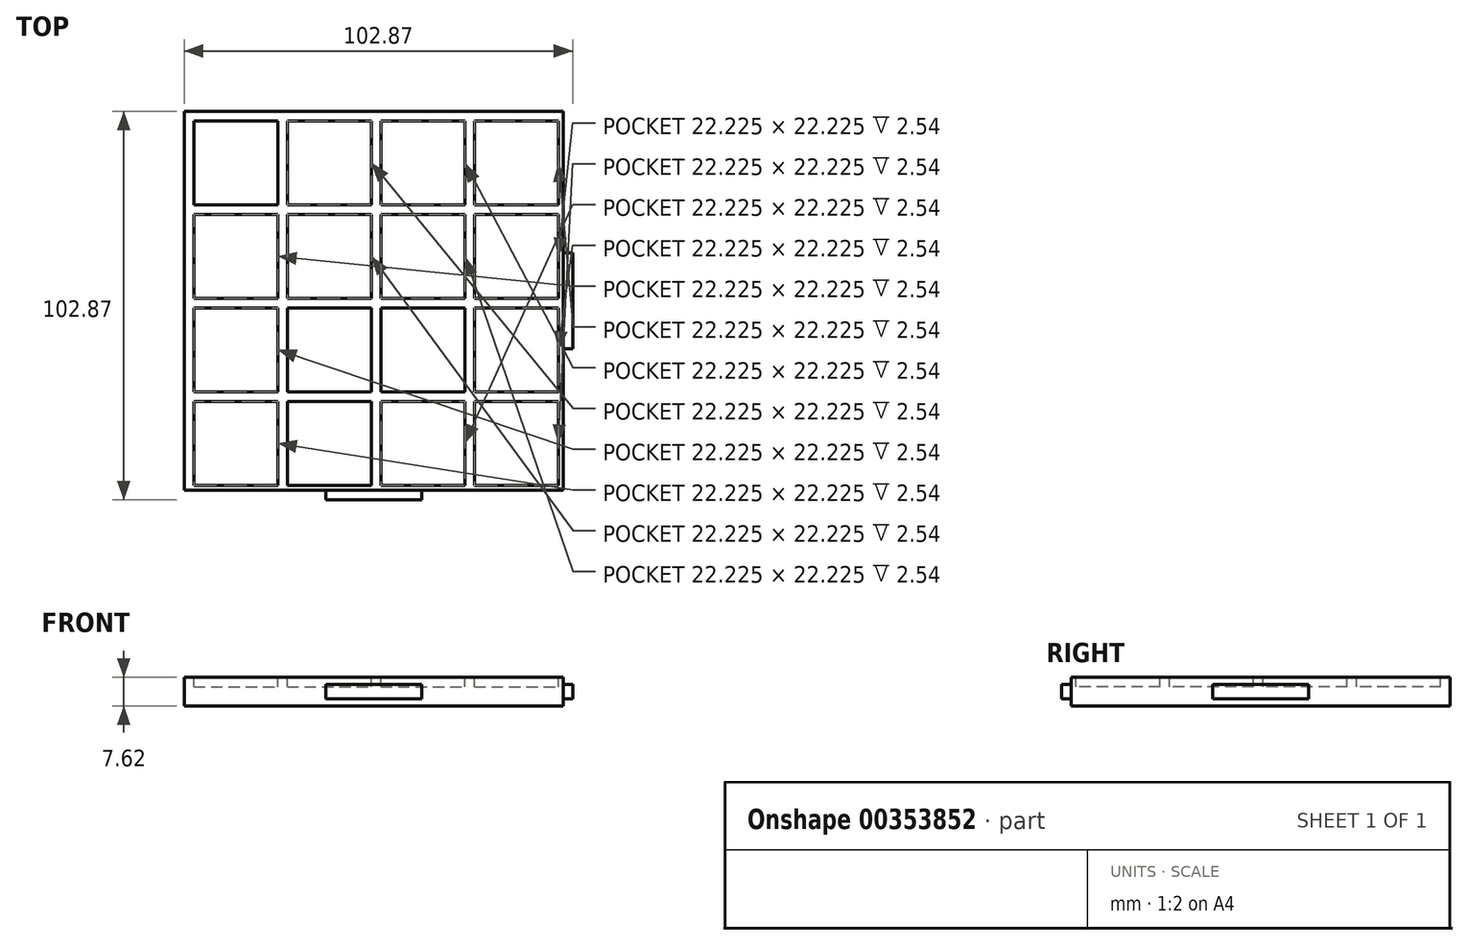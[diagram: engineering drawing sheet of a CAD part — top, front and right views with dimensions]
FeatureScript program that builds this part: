
annotation { "Feature Type Name" : "Feature", "Feature Type Description" : "" }
export const myFeature = defineFeature(function(context is Context, id is Id, definition is map)
    precondition{}
    {
        {
            var Q0;
            Q0=qCreatedBy(makeId("Top.planeOp"),FACE);
            var sketch = newSketch(context, id + "F0", { "sketchPlane" : qUnion([Q0])});
            skLineSegment(sketch, "E0.bottom", {"start": v(0, 0) * mm, "end": v(100.33, 0) * mm});
            skLineSegment(sketch, "E0.top", {"start": v(0, 100.33) * mm, "end": v(100.33, 100.33) * mm});
            skLineSegment(sketch, "E0.left", {"start": v(0, 0) * mm, "end": v(0, 100.33) * mm});
            skLineSegment(sketch, "E0.right", {"start": v(100.33, 0) * mm, "end": v(100.33, 100.33) * mm});
            skSolve(sketch);
        }
        {
            var Q0;
            Q0 = qSketchRegion(id + "F0", true);
            extrude(context, id + "F1", {"entities" : qUnion([Q0]), "oppositeDirection" : true, "depth" : 7.62 * mm});
        }
        {
            var Q0;
            Q0=qCreatedBy(makeId("Top.planeOp"),FACE);
            var sketch = newSketch(context, id + "F2", { "sketchPlane" : qUnion([Q0])});
            skLineSegment(sketch, "E1.bottom", {"start": v(2.54, 97.8) * mm, "end": v(24.77, 97.8) * mm});
            skLineSegment(sketch, "E1.top", {"start": v(2.54, 75.57) * mm, "end": v(24.77, 75.57) * mm});
            skLineSegment(sketch, "E1.left", {"start": v(2.54, 97.8) * mm, "end": v(2.54, 75.57) * mm});
            skLineSegment(sketch, "E1.right", {"start": v(24.77, 97.8) * mm, "end": v(24.77, 75.56) * mm});
            skLineSegment(sketch, "E2.bottom", {"start": v(27.3, 97.8) * mm, "end": v(49.53, 97.8) * mm});
            skLineSegment(sketch, "E2.top", {"start": v(27.3, 75.56) * mm, "end": v(49.53, 75.57) * mm});
            skLineSegment(sketch, "E2.left", {"start": v(27.3, 97.8) * mm, "end": v(27.3, 75.56) * mm});
            skLineSegment(sketch, "E2.right", {"start": v(49.53, 97.8) * mm, "end": v(49.53, 75.56) * mm});
            skLineSegment(sketch, "E3.bottom", {"start": v(52.07, 97.8) * mm, "end": v(74.3, 97.8) * mm});
            skLineSegment(sketch, "E3.top", {"start": v(52.07, 75.57) * mm, "end": v(74.3, 75.57) * mm});
            skLineSegment(sketch, "E3.left", {"start": v(52.07, 97.8) * mm, "end": v(52.07, 75.57) * mm});
            skLineSegment(sketch, "E3.right", {"start": v(74.3, 97.8) * mm, "end": v(74.3, 75.57) * mm});
            skLineSegment(sketch, "E4.bottom", {"start": v(76.84, 97.8) * mm, "end": v(99.06, 97.8) * mm});
            skLineSegment(sketch, "E4.top", {"start": v(76.84, 75.57) * mm, "end": v(99.06, 75.56) * mm});
            skLineSegment(sketch, "E4.left", {"start": v(76.84, 97.8) * mm, "end": v(76.84, 75.57) * mm});
            skLineSegment(sketch, "E4.right", {"start": v(99.06, 97.8) * mm, "end": v(99.06, 75.57) * mm});
            skLineSegment(sketch, "E5.bottom", {"start": v(2.54, 73.03) * mm, "end": v(24.77, 73.03) * mm});
            skLineSegment(sketch, "E5.top", {"start": v(2.54, 50.8) * mm, "end": v(24.76, 50.8) * mm});
            skLineSegment(sketch, "E5.left", {"start": v(2.54, 73.03) * mm, "end": v(2.54, 50.8) * mm});
            skLineSegment(sketch, "E5.right", {"start": v(24.76, 73.03) * mm, "end": v(24.76, 50.8) * mm});
            skLineSegment(sketch, "E6.bottom", {"start": v(2.54, 48.26) * mm, "end": v(24.77, 48.26) * mm});
            skLineSegment(sketch, "E6.top", {"start": v(2.54, 26.04) * mm, "end": v(24.77, 26.04) * mm});
            skLineSegment(sketch, "E6.left", {"start": v(2.54, 48.26) * mm, "end": v(2.54, 26.04) * mm});
            skLineSegment(sketch, "E6.right", {"start": v(24.77, 48.26) * mm, "end": v(24.77, 26.04) * mm});
            skLineSegment(sketch, "E7.bottom", {"start": v(2.54, 23.5) * mm, "end": v(24.77, 23.5) * mm});
            skLineSegment(sketch, "E7.top", {"start": v(2.54, 1.27) * mm, "end": v(24.76, 1.27) * mm});
            skLineSegment(sketch, "E7.left", {"start": v(2.54, 23.5) * mm, "end": v(2.54, 1.27) * mm});
            skLineSegment(sketch, "E7.right", {"start": v(24.77, 23.5) * mm, "end": v(24.77, 1.27) * mm});
            skLineSegment(sketch, "E8.bottom", {"start": v(27.3, 73.02) * mm, "end": v(49.53, 73.02) * mm});
            skLineSegment(sketch, "E8.top", {"start": v(27.3, 50.8) * mm, "end": v(49.53, 50.8) * mm});
            skLineSegment(sketch, "E8.left", {"start": v(27.3, 73.02) * mm, "end": v(27.3, 50.8) * mm});
            skLineSegment(sketch, "E8.right", {"start": v(49.53, 73.02) * mm, "end": v(49.53, 50.8) * mm});
            skLineSegment(sketch, "E9.bottom", {"start": v(52.07, 73.03) * mm, "end": v(74.3, 73.03) * mm});
            skLineSegment(sketch, "E9.top", {"start": v(52.07, 50.8) * mm, "end": v(74.3, 50.8) * mm});
            skLineSegment(sketch, "E9.left", {"start": v(52.07, 73.03) * mm, "end": v(52.07, 50.8) * mm});
            skLineSegment(sketch, "E9.right", {"start": v(74.3, 73.03) * mm, "end": v(74.3, 50.8) * mm});
            skLineSegment(sketch, "E10.bottom", {"start": v(76.83, 73.03) * mm, "end": v(99.06, 73.03) * mm});
            skLineSegment(sketch, "E10.top", {"start": v(76.83, 50.8) * mm, "end": v(99.06, 50.8) * mm});
            skLineSegment(sketch, "E10.left", {"start": v(76.83, 73.03) * mm, "end": v(76.83, 50.8) * mm});
            skLineSegment(sketch, "E10.right", {"start": v(99.06, 73.03) * mm, "end": v(99.06, 50.8) * mm});
            skLineSegment(sketch, "E11.bottom", {"start": v(27.3, 48.26) * mm, "end": v(49.53, 48.26) * mm});
            skLineSegment(sketch, "E11.top", {"start": v(27.3, 26.03) * mm, "end": v(49.53, 26.03) * mm});
            skLineSegment(sketch, "E11.left", {"start": v(27.3, 48.26) * mm, "end": v(27.3, 26.03) * mm});
            skLineSegment(sketch, "E11.right", {"start": v(49.53, 48.26) * mm, "end": v(49.53, 26.03) * mm});
            skLineSegment(sketch, "E12.bottom", {"start": v(27.3, 23.5) * mm, "end": v(49.53, 23.5) * mm});
            skLineSegment(sketch, "E12.top", {"start": v(27.3, 1.27) * mm, "end": v(49.53, 1.27) * mm});
            skLineSegment(sketch, "E12.left", {"start": v(27.3, 23.5) * mm, "end": v(27.3, 1.27) * mm});
            skLineSegment(sketch, "E12.right", {"start": v(49.53, 23.5) * mm, "end": v(49.53, 1.27) * mm});
            skLineSegment(sketch, "E13.bottom", {"start": v(52.07, 48.26) * mm, "end": v(74.3, 48.26) * mm});
            skLineSegment(sketch, "E13.top", {"start": v(52.07, 26.03) * mm, "end": v(74.3, 26.03) * mm});
            skLineSegment(sketch, "E13.left", {"start": v(52.07, 48.26) * mm, "end": v(52.07, 26.03) * mm});
            skLineSegment(sketch, "E13.right", {"start": v(74.3, 48.26) * mm, "end": v(74.3, 26.03) * mm});
            skLineSegment(sketch, "E14.bottom", {"start": v(76.84, 48.26) * mm, "end": v(99.06, 48.26) * mm});
            skLineSegment(sketch, "E14.top", {"start": v(76.84, 26.04) * mm, "end": v(99.06, 26.03) * mm});
            skLineSegment(sketch, "E14.left", {"start": v(76.84, 48.26) * mm, "end": v(76.84, 26.04) * mm});
            skLineSegment(sketch, "E14.right", {"start": v(99.06, 48.26) * mm, "end": v(99.06, 26.03) * mm});
            skLineSegment(sketch, "E15.bottom", {"start": v(52.07, 23.5) * mm, "end": v(74.3, 23.5) * mm});
            skLineSegment(sketch, "E15.top", {"start": v(52.07, 1.27) * mm, "end": v(74.3, 1.27) * mm});
            skLineSegment(sketch, "E15.left", {"start": v(52.07, 23.5) * mm, "end": v(52.07, 1.27) * mm});
            skLineSegment(sketch, "E15.right", {"start": v(74.3, 23.5) * mm, "end": v(74.3, 1.27) * mm});
            skLineSegment(sketch, "E16.bottom", {"start": v(76.84, 23.5) * mm, "end": v(99.06, 23.5) * mm});
            skLineSegment(sketch, "E16.top", {"start": v(76.84, 1.27) * mm, "end": v(99.06, 1.27) * mm});
            skLineSegment(sketch, "E16.left", {"start": v(76.84, 23.5) * mm, "end": v(76.84, 1.27) * mm});
            skLineSegment(sketch, "E16.right", {"start": v(99.06, 23.5) * mm, "end": v(99.06, 1.27) * mm});
            skSolve(sketch);
        }
        {
            var Q0;
            Q0 = qSketchRegion(id + "F2", true);
            extrude(context, id + "F3", {"entities" : qUnion([Q0]), "operationType" : NewBodyOperationType.REMOVE, "oppositeDirection" : true, "depth" : 2.54 * mm});
        }
        {
            var Q0;
            Q0=makeQuery(id+"F1.opExtrude","SWEPT_FACE",FACE,{"disambiguationData":[OSD([sQuery(id+"F0.wireOp",EDGE,"E0.bottom")])]});
            var sketch = newSketch(context, id + "F4", { "sketchPlane" : qUnion([Q0])});
            skLineSegment(sketch, "E17.bottom", {"start": v(37.47, -1.9) * mm, "end": v(62.87, -1.9) * mm});
            skLineSegment(sketch, "E17.top", {"start": v(37.47, -5.71) * mm, "end": v(62.87, -5.71) * mm});
            skLineSegment(sketch, "E17.left", {"start": v(37.47, -1.9) * mm, "end": v(37.47, -5.71) * mm});
            skLineSegment(sketch, "E17.right", {"start": v(62.87, -1.9) * mm, "end": v(62.87, -5.71) * mm});
            skLineSegment(sketch, "E18", {"start": v(37.47, -1.9) * mm, "end": v(0, -1.9) * mm, "construction": true});
            skLineSegment(sketch, "E19", {"start": v(62.87, -3.8) * mm, "end": v(100.33, -3.8) * mm, "construction": true});
            skLineSegment(sketch, "E20", {"start": v(52.96, -1.9) * mm, "end": v(52.96, 0) * mm, "construction": true});
            skLineSegment(sketch, "E21", {"start": v(54.09, -5.71) * mm, "end": v(54.09, -7.62) * mm, "construction": true});
            skSolve(sketch);
        }
        {
            var Q0;
            Q0=makeQuery(id+"F1.opExtrude","SWEPT_FACE",FACE,{"disambiguationData":[OSD([sQuery(id+"F0.wireOp",EDGE,"E0.right")])]});
            var sketch = newSketch(context, id + "F5", { "sketchPlane" : qUnion([Q0])});
            skLineSegment(sketch, "E22.bottom", {"start": v(37.46, -1.9) * mm, "end": v(62.86, -1.9) * mm});
            skLineSegment(sketch, "E22.top", {"start": v(37.46, -5.71) * mm, "end": v(62.86, -5.71) * mm});
            skLineSegment(sketch, "E22.left", {"start": v(37.46, -1.9) * mm, "end": v(37.46, -5.71) * mm});
            skLineSegment(sketch, "E22.right", {"start": v(62.86, -1.9) * mm, "end": v(62.86, -5.71) * mm});
            skLineSegment(sketch, "E23", {"start": v(0, -3.81) * mm, "end": v(37.46, -3.81) * mm, "construction": true});
            skLineSegment(sketch, "E24", {"start": v(62.86, -3.81) * mm, "end": v(100.33, -3.81) * mm, "construction": true});
            skLineSegment(sketch, "E25", {"start": v(47.77, -5.71) * mm, "end": v(47.77, -7.62) * mm, "construction": true});
            skPoint(sketch, "E25.endSnap0", {"position": v(50.16, -7.62) * mm});
            skLineSegment(sketch, "E26", {"start": v(48.6, -1.9) * mm, "end": v(48.6, 0) * mm, "construction": true});
            skSolve(sketch);
        }
        {
            var Q0;
            Q0=makeQuery(id+"F5.imprint","IMPRINT",FACE,{"disambiguationData":[TD([[makeQuery(id+"F5.imprint","IMPRINT",EDGE,{"derivedFrom":sQuery(id+"F5.wireOp",EDGE,"E22.bottom")}),-1.0]])]});
            extrude(context, id + "F6", {"entities" : qUnion([Q0]), "operationType" : NewBodyOperationType.ADD, "depth" : 2.54 * mm});
        }
        {
            var Q0;
            Q0=makeQuery(id+"F4.imprint","IMPRINT",FACE,{"disambiguationData":[TD([[makeQuery(id+"F4.imprint","IMPRINT",EDGE,{"derivedFrom":sQuery(id+"F4.wireOp",EDGE,"E17.bottom")}),-1.0]])]});
            extrude(context, id + "F7", {"entities" : qUnion([Q0]), "operationType" : NewBodyOperationType.ADD, "depth" : 2.54 * mm});
        }
    });
